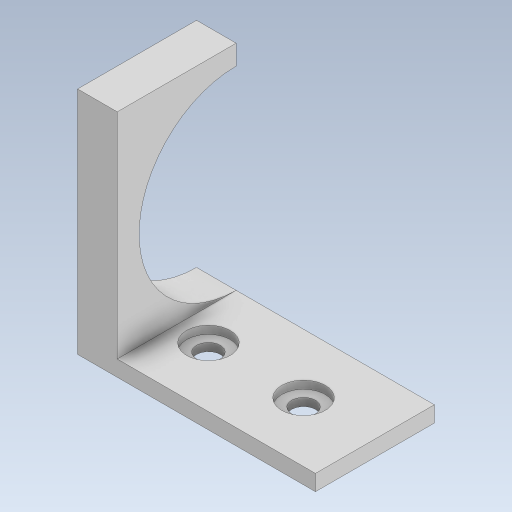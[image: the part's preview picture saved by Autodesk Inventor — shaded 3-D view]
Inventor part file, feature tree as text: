
AUTODESK INVENTOR PART (.ipt)
format: ipt  version: 2023.5 (Build 275446000, 446)  size: 317,440 bytes
history: native  units: in
note: dims shown in document units (in); Inventor stores cm internally (conversion verified against a paired STEP export)
features: extrude x5, sketch x3
ambient origin geometry x8: Origin, YZ Plane, XZ Plane, XY Plane, X Axis, Y Axis, Z Axis, Center Point
bodies: Solid1 (feature_tree)
feature tree (8):
  sketch  "Sketch1"  dims[d0=1.1811in d1=0.5906in]
  extrude  "Extrusion1"  Depth=0.5906in
  extrude  "Extrusion2"  Depth=0.0787in
  extrude  "Extrusion3"  Depth=0.2362in
  extrude  "Extrusion4"  Depth=0.0787in TaperAngle=0.0deg
  extrude  "Extrusion5"  Depth=1.1417in TaperAngle=0.0deg
  sketch  "Sketch2"  dims[d2=0.0787in d3=0.1181in]
  sketch  "Sketch3"  dims[d4=0.2165in d5=0.2362in d6=0.0787in d7=0.0in d8=1.1417in d9=0.0in d10=0.0394in d11=0.0in d13=0.0787in d14=0.0in d16=0.9646in d17=0.4823in d18=0.1181in d19=0.0in d15=0.0197in]
